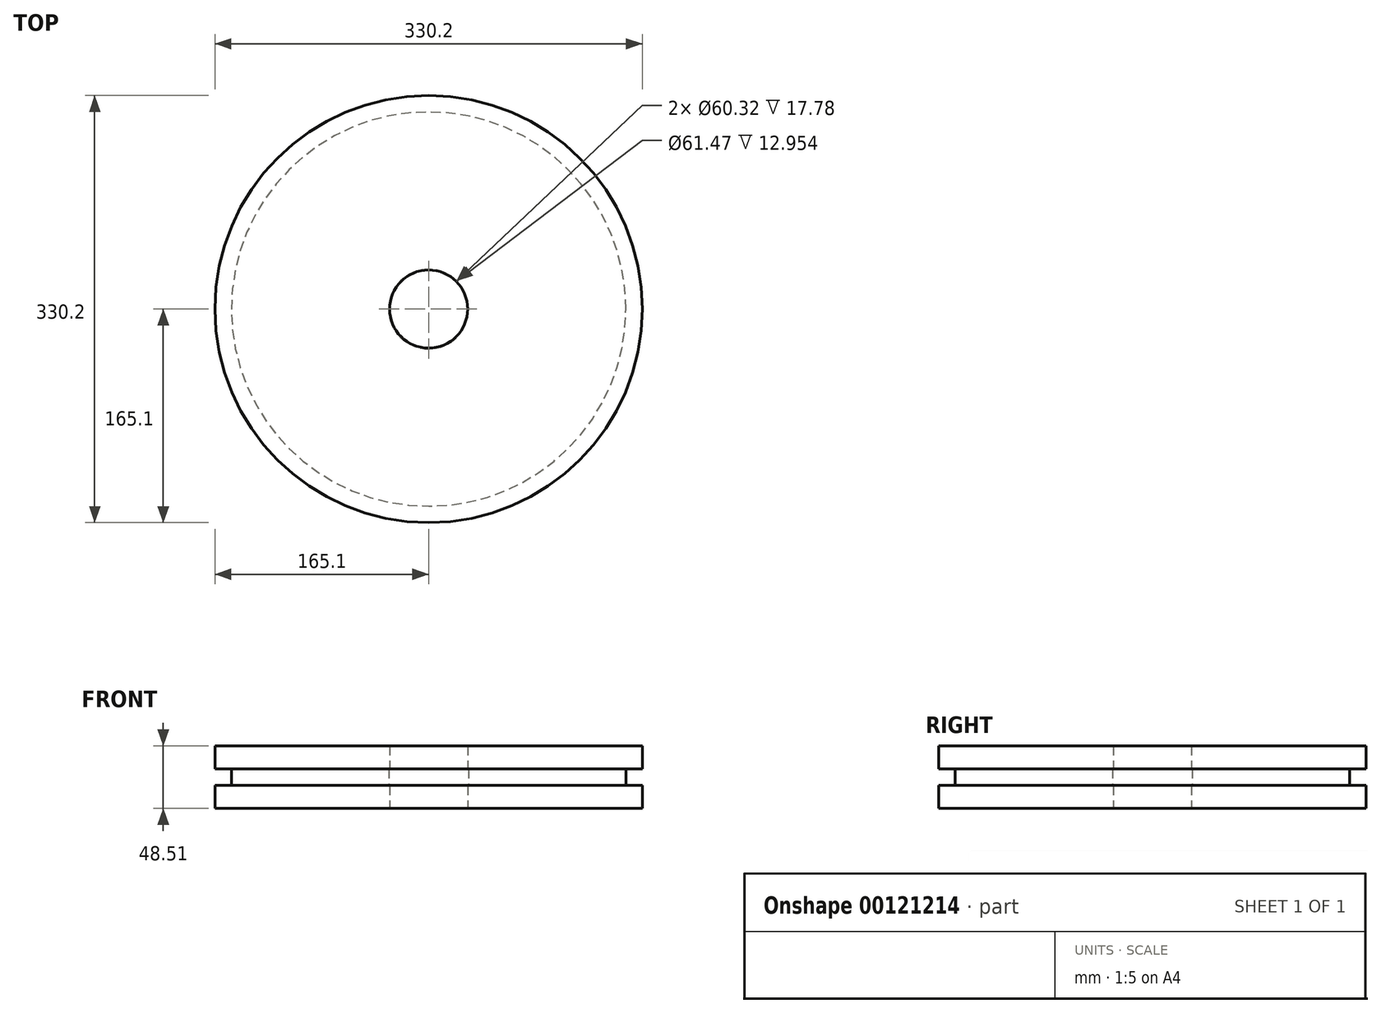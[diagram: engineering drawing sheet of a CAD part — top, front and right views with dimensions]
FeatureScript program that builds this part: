
annotation { "Feature Type Name" : "Feature", "Feature Type Description" : "" }
export const myFeature = defineFeature(function(context is Context, id is Id, definition is map)
    precondition{}
    {
        {
            var Q0;
            Q0=qCreatedBy(makeId("Top.planeOp"),FACE);
            var sketch = newSketch(context, id + "F0", { "sketchPlane" : qUnion([Q0])});
            skCircle(sketch, "E0", {"center": v(0, 0) * mm, "radius": 152.4 * mm});
            skCircle(sketch, "E1", {"center": v(0, 0) * mm, "radius": 30.73 * mm});
            skSolve(sketch);
        }
        {
            var Q0;
            Q0 = qSketchRegion(id + "F0", true);
            extrude(context, id + "F1", {"entities" : qUnion([Q0]), "depth" : 12.95 * mm});
        }
        {
            var Q0;
            Q0=makeQuery(id+"F1.opExtrude","CAP_FACE",FACE,{"disambiguationData":[OSD([sQuery(id+"F0.wireOp",EDGE,"E0"),sQuery(id+"F0.wireOp",EDGE,"E1")])],"isStart":false});
            var sketch = newSketch(context, id + "F2", { "sketchPlane" : qUnion([Q0])});
            skCircle(sketch, "E2", {"center": v(0, 0) * mm, "radius": 165.1 * mm});
            skSolve(sketch);
        }
        {
            var Q0;
            Q0 = qSketchRegion(id + "F2", true);
            extrude(context, id + "F3", {"entities" : qUnion([Q0]), "operationType" : NewBodyOperationType.ADD, "depth" : 17.78 * mm});
        }
        {
            var Q0;
            Q0=makeQuery(id+"F1.opExtrude","CAP_FACE",FACE,{"disambiguationData":[OSD([sQuery(id+"F0.wireOp",EDGE,"E0"),sQuery(id+"F0.wireOp",EDGE,"E1")])],"isStart":true});
            var sketch = newSketch(context, id + "F4", { "sketchPlane" : qUnion([Q0])});
            skCircle(sketch, "E3", {"center": v(0, 0) * mm, "radius": 165.1 * mm});
            skSolve(sketch);
        }
        {
            var Q0;
            Q0 = qSketchRegion(id + "F4", true);
            extrude(context, id + "F5", {"entities" : qUnion([Q0]), "operationType" : NewBodyOperationType.ADD, "depth" : 17.78 * mm});
        }
        {
            var Q0;
            Q0=makeQuery(id+"F5.opExtrude","CAP_FACE",FACE,{"disambiguationData":[OSD([sQuery(id+"F4.wireOp",EDGE,"E3")])],"isStart":false});
            var sketch = newSketch(context, id + "F6", { "sketchPlane" : qUnion([Q0])});
            skCircle(sketch, "E4", {"center": v(0, 0) * mm, "radius": 30.16 * mm});
            skSolve(sketch);
        }
        {
            var Q0;
            Q0 = qSketchRegion(id + "F6", true);
            extrude(context, id + "F7", {"entities" : qUnion([Q0]), "operationType" : NewBodyOperationType.REMOVE, "oppositeDirection" : true, "depth" : 62.67 * mm});
        }
    });
